# Revit family: GM5B
name_source: partatom
category: Air Terminals
revit_build: Autodesk Revit MEP 2012 (Build: 20110309_2315(x64)
units: mm (PartAtom-declared; Revit-internal decimal feet)

## types (4) — shared parameters
Ancho barra = 1/32"
Largo barra = 1/4"
Manufacturer = INNES
Máxima presión estática = 0.00 in-wg
Máxima velocidad de cuello = 0 FPM
Mínima presión estática = 0.00 in-wg
Mínima velocidad de cuello = 0 FPM
Separacion = 1/2"
URL = http://www.innes.com.mx

## per-type parameters (varying)
| type | A Largo | A barras | A parilla | B | Height | Largo parilla | No. de elementos | No. de elementos barras | Width |
| GM5B-24-16 | 23 7/8" | 22 9/16" | 23" | 15 7/8" | 17 7/8" | 15" | 46 | 30 | 25 7/8" |
| GM5B-25-17 | 24 7/8" | 23 9/16" | 24" | 16 7/8" | 18 7/8" | 16" | 48 | 32 | 26 7/8" |
| GM5B-26-18 | 25 7/8" | 24 9/16" | 25" | 17 7/8" | 19 7/8" | 17" | 50 | 34 | 27 7/8" |
| GM5B-27-19 | 26 7/8" | 25 9/16" | 26" | 18 7/8" | 20 7/8" | 18" | 52 | 36 | 28 7/8" |

## geometry (parser evidence)
native form markers: Blend x3, Sweep x5
no freeform markers — native parametric forms only
